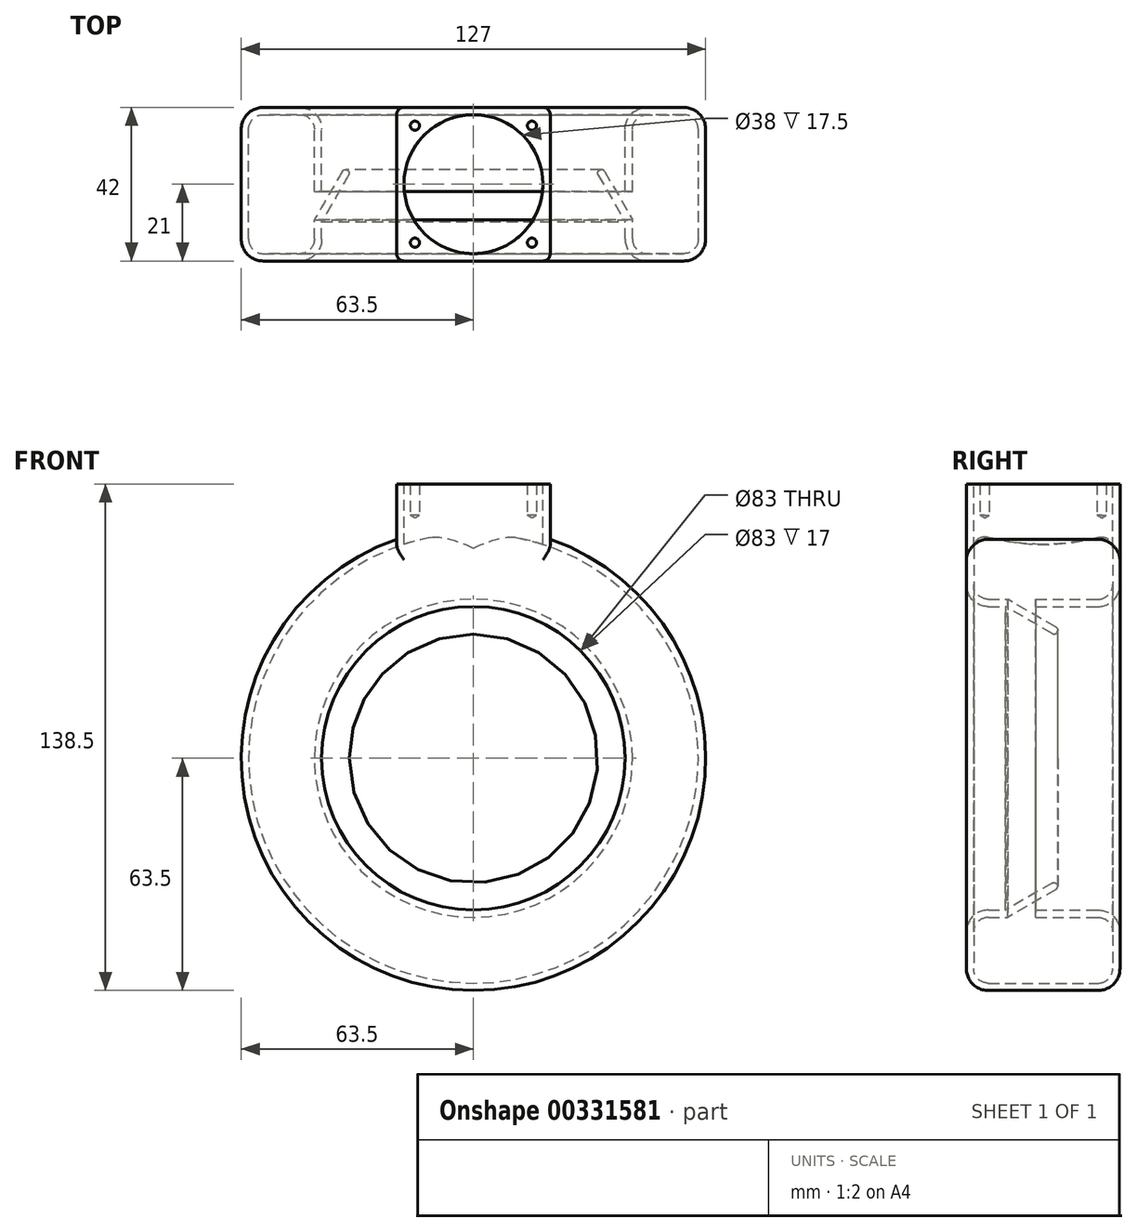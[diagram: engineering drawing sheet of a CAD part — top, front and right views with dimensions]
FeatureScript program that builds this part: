
annotation { "Feature Type Name" : "Feature", "Feature Type Description" : "" }
export const myFeature = defineFeature(function(context is Context, id is Id, definition is map)
    precondition{}
    {
        {
            var Q0;
            Q0=qCreatedBy(makeId("Top.planeOp"),FACE);
            var sketch = newSketch(context, id + "F0", { "sketchPlane" : qUnion([Q0])});
            skLineSegment(sketch, "E0.bottom", {"start": v(-7.5, 20) * mm, "end": v(2.5, 20) * mm, "construction": true});
            skLineSegment(sketch, "E0.top", {"start": v(-7.5, -20) * mm, "end": v(2.5, -20) * mm, "construction": true});
            skLineSegment(sketch, "E0.left", {"start": v(-12.5, 15) * mm, "end": v(-12.5, -15) * mm, "construction": true});
            skPoint(sketch, "E0.middle", {"position": v(0, 0) * mm});
            skPoint(sketch, "E1.visualSharp", {"position": v(-12.5, 20) * mm});
            skArc(sketch, "E1.filletArc", {"start": v(-7.5, 20) * mm, "mid": v(-11.04, 18.54) * mm, "end": v(-12.5, 15) * mm, "construction": true});
            skPoint(sketch, "E2.visualSharp", {"position": v(12.5, 20) * mm});
            skArc(sketch, "E2.filletArc", {"start": v(7.5, 15) * mm, "mid": v(6.04, 18.54) * mm, "end": v(2.5, 20) * mm, "construction": true});
            skPoint(sketch, "E3.visualSharp", {"position": v(12.5, -20) * mm});
            skArc(sketch, "E3.filletArc", {"start": v(2.5, -20) * mm, "mid": v(6.04, -18.54) * mm, "end": v(7.5, -15) * mm, "construction": true});
            skPoint(sketch, "E4.visualSharp", {"position": v(-12.5, -20) * mm});
            skArc(sketch, "E4.filletArc", {"start": v(-12.5, -15) * mm, "mid": v(-11.04, -18.54) * mm, "end": v(-7.5, -20) * mm, "construction": true});
            skLineSegment(sketch, "E5", {"start": v(7.5, -10) * mm, "end": v(15, 3) * mm, "construction": true});
            skLineSegment(sketch, "E6", {"start": v(7.5, 15) * mm, "end": v(7.5, -2) * mm, "construction": true});
            skLineSegment(sketch, "E7", {"start": v(7.5, -10) * mm, "end": v(7.5, -15) * mm, "construction": true});
            skLineSegment(sketch, "E8.0", {"start": v(8.5, 15) * mm, "end": v(8.5, -2) * mm});
            skArc(sketch, "E8.1", {"start": v(8.5, 15) * mm, "mid": v(6.74, 19.24) * mm, "end": v(2.5, 21) * mm});
            skLineSegment(sketch, "E8.2", {"start": v(-7.5, 21) * mm, "end": v(2.5, 21) * mm});
            skArc(sketch, "E8.3", {"start": v(-7.5, 21) * mm, "mid": v(-11.74, 19.24) * mm, "end": v(-13.5, 15) * mm});
            skLineSegment(sketch, "E8.4", {"start": v(-13.5, 15) * mm, "end": v(-13.5, -15) * mm});
            skArc(sketch, "E8.5", {"start": v(-13.5, -15) * mm, "mid": v(-11.74, -19.24) * mm, "end": v(-7.5, -21) * mm});
            skLineSegment(sketch, "E8.6", {"start": v(8.5, -10.27) * mm, "end": v(15.87, 2.5) * mm});
            skLineSegment(sketch, "E8.7", {"start": v(8.5, -10.27) * mm, "end": v(8.5, -15) * mm});
            skArc(sketch, "E8.8", {"start": v(2.5, -21) * mm, "mid": v(6.74, -19.24) * mm, "end": v(8.5, -15) * mm});
            skLineSegment(sketch, "E8.9", {"start": v(-7.5, -21) * mm, "end": v(2.5, -21) * mm});
            skLineSegment(sketch, "E9.0", {"start": v(6.5, 15) * mm, "end": v(6.5, -2) * mm});
            skArc(sketch, "E9.1", {"start": v(6.5, 15) * mm, "mid": v(5.33, 17.83) * mm, "end": v(2.5, 19) * mm});
            skLineSegment(sketch, "E9.2", {"start": v(-7.5, 19) * mm, "end": v(2.5, 19) * mm});
            skArc(sketch, "E9.3", {"start": v(-7.5, 19) * mm, "mid": v(-10.33, 17.83) * mm, "end": v(-11.5, 15) * mm});
            skLineSegment(sketch, "E9.4", {"start": v(-11.5, 15) * mm, "end": v(-11.5, -15) * mm});
            skArc(sketch, "E9.5", {"start": v(-11.5, -15) * mm, "mid": v(-10.33, -17.83) * mm, "end": v(-7.5, -19) * mm});
            skLineSegment(sketch, "E9.6", {"start": v(6.5, -9.73) * mm, "end": v(14.13, 3.5) * mm});
            skLineSegment(sketch, "E9.7", {"start": v(6.5, -9.73) * mm, "end": v(6.5, -15) * mm});
            skArc(sketch, "E9.8", {"start": v(2.5, -19) * mm, "mid": v(5.33, -17.83) * mm, "end": v(6.5, -15) * mm});
            skLineSegment(sketch, "E9.9", {"start": v(-7.5, -19) * mm, "end": v(2.5, -19) * mm});
            skLineSegment(sketch, "E10", {"start": v(6.5, -2) * mm, "end": v(8.5, -2) * mm});
            skArc(sketch, "E11", {"start": v(15.87, 2.5) * mm, "mid": v(15.5, 3.86) * mm, "end": v(14.13, 3.5) * mm});
            skSolve(sketch);
        }
        {
            var Q0;
            Q0=qCreatedBy(makeId("Front.planeOp"),FACE);
            var sketch = newSketch(context, id + "F1", { "sketchPlane" : qUnion([Q0])});
            skLineSegment(sketch, "E12", {"start": v(0, 0) * mm, "end": v(0, 0) * mm});
            skLineSegment(sketch, "E13", {"start": v(50, -50) * mm, "end": v(50, -50) * mm});
            skLineSegment(sketch, "E14", {"start": v(100, 0) * mm, "end": v(100, 0) * mm});
            skLineSegment(sketch, "E15", {"start": v(50, 50) * mm, "end": v(50, 50) * mm});
            skPoint(sketch, "E16.visualSharp", {"position": v(0, 50) * mm});
            skArc(sketch, "E16.filletArc", {"start": v(50, 50) * mm, "mid": v(14.64, 35.36) * mm, "end": v(0, 0) * mm});
            skPoint(sketch, "E17.visualSharp", {"position": v(100, 50) * mm});
            skArc(sketch, "E17.filletArc", {"start": v(100, 0) * mm, "mid": v(85.36, 35.36) * mm, "end": v(50, 50) * mm});
            skPoint(sketch, "E18.visualSharp", {"position": v(100, -50) * mm});
            skArc(sketch, "E18.filletArc", {"start": v(50, -50) * mm, "mid": v(85.36, -35.36) * mm, "end": v(100, 0) * mm});
            skPoint(sketch, "E19.visualSharp", {"position": v(0, -50) * mm});
            skArc(sketch, "E19.filletArc", {"start": v(0, 0) * mm, "mid": v(14.64, -35.36) * mm, "end": v(50, -50) * mm});
            skSolve(sketch);
        }
        {
            var Q0;
            Q0=makeQuery(id+"F0.imprint","IMPRINT",FACE,{"disambiguationData":[TD([[makeQuery(id+"F0.imprint","IMPRINT",EDGE,{"derivedFrom":sQuery(id+"F0.wireOp",EDGE,"E8.0")}),-1.0]])]});
            var Q1;
            Q1=sQuery(id+"F1.wireOp",EDGE,"E16.filletArc");
            var Q2;
            Q2=sQuery(id+"F1.wireOp",EDGE,"E18.filletArc");
            var Q3;
            Q3=sQuery(id+"F1.wireOp",EDGE,"E17.filletArc");
            var Q4;
            Q4=sQuery(id+"F1.wireOp",EDGE,"E19.filletArc");
            sweep(context, id + "F2", {"profiles" : qUnion([Q0]), "path" : qUnion([Q1, Q2, Q3, Q4])});
        }
        {
            var Q0;
            Q0=qCreatedBy(makeId("Top.planeOp"),FACE);
            cPlane(context, id + "F3", {"entities" : qUnion([Q0]), "cplaneType" : CPlaneType.OFFSET, "offset" : 75 * mm, "width" : 150 * mm, "height" : 150 * mm});
        }
        {
            var Q0;
            Q0=qCreatedBy(id+"F3.planeOp",FACE);
            var sketch = newSketch(context, id + "F4", { "sketchPlane" : qUnion([Q0])});
            skLineSegment(sketch, "E20.0", {"start": v(-13.5, 15) * mm, "end": v(113.5, 15) * mm, "construction": true});
            skLineSegment(sketch, "E20.1", {"start": v(-13.5, -15) * mm, "end": v(113.5, -15) * mm, "construction": true});
            skLineSegment(sketch, "E21", {"start": v(50, 49.18) * mm, "end": v(50, -47.1) * mm, "construction": true});
            skPoint(sketch, "E21.startSnap0", {"position": v(50, 15) * mm});
            skLineSegment(sketch, "E22", {"start": v(0, 0) * mm, "end": v(109, 0) * mm, "construction": true});
            skCircle(sketch, "E23", {"center": v(50, 0) * mm, "radius": 19 * mm});
            skLineSegment(sketch, "E24.bottom", {"start": v(71, -21) * mm, "end": v(29, -21) * mm});
            skLineSegment(sketch, "E24.top", {"start": v(71, 21) * mm, "end": v(29, 21) * mm});
            skLineSegment(sketch, "E24.left", {"start": v(71, -21) * mm, "end": v(71, 21) * mm});
            skLineSegment(sketch, "E24.right", {"start": v(29, -21) * mm, "end": v(29, 21) * mm});
            skSolve(sketch);
        }
        {
            var Q0;
            Q0 = qSketchRegion(id + "F4", true);
            extrude(context, id + "F5", {"entities" : qUnion([Q0]), "operationType" : NewBodyOperationType.ADD, "endBound" : BoundingType.UP_TO_NEXT, "oppositeDirection" : true, "depth" : 25 * mm});
        }
        {
            var Q0;
            Q0=makeQuery(id+"F5.opExtrude","CAP_FACE",FACE,{"disambiguationData":[OSD([sQuery(id+"F4.wireOp",EDGE,"E23"),sQuery(id+"F4.wireOp",EDGE,"E24.bottom"),sQuery(id+"F4.wireOp",EDGE,"E24.top"),sQuery(id+"F4.wireOp",EDGE,"E24.left"),sQuery(id+"F4.wireOp",EDGE,"E24.right")])],"isStart":true});
            var sketch = newSketch(context, id + "F6", { "sketchPlane" : qUnion([Q0])});
            skCircle(sketch, "E25.0", {"center": v(50, 0) * mm, "radius": 19 * mm});
            skSolve(sketch);
        }
        {
            var Q0;
            Q0 = qSketchRegion(id + "F6", true);
            extrude(context, id + "F7", {"entities" : qUnion([Q0]), "operationType" : NewBodyOperationType.REMOVE, "oppositeDirection" : true, "depth" : 25 * mm});
        }
        {
            var Q0;
            Q0=makeQuery(id+"F5.opExtrude","CAP_FACE",FACE,{"disambiguationData":[OSD([sQuery(id+"F4.wireOp",EDGE,"E23"),sQuery(id+"F4.wireOp",EDGE,"E24.bottom"),sQuery(id+"F4.wireOp",EDGE,"E24.top"),sQuery(id+"F4.wireOp",EDGE,"E24.left"),sQuery(id+"F4.wireOp",EDGE,"E24.right")])],"isStart":true});
            var sketch = newSketch(context, id + "F8", { "sketchPlane" : qUnion([Q0])});
            skCircle(sketch, "E26.0", {"center": v(50, 0) * mm, "radius": 19 * mm, "construction": true});
            skLineSegment(sketch, "E27.bottom", {"start": v(66, 16) * mm, "end": v(34, 16) * mm, "construction": true});
            skLineSegment(sketch, "E27.top", {"start": v(66, -16) * mm, "end": v(34, -16) * mm, "construction": true});
            skLineSegment(sketch, "E27.left", {"start": v(66, 16) * mm, "end": v(66, -16) * mm, "construction": true});
            skLineSegment(sketch, "E27.right", {"start": v(34, 16) * mm, "end": v(34, -16) * mm, "construction": true});
            skPoint(sketch, "E28", {"position": v(34, 16) * mm});
            skPoint(sketch, "E29", {"position": v(66, 16) * mm});
            skPoint(sketch, "E30", {"position": v(66, -16) * mm});
            skPoint(sketch, "E31", {"position": v(34, -16) * mm});
            skSolve(sketch);
        }
        {
            var Q0;
            Q0=sQuery(id+"F8.wireOp",VERTEX,"E27.bottom.end");
            var Q1;
            Q1=sQuery(id+"F8.wireOp",VERTEX,"E29");
            var Q2;
            Q2=sQuery(id+"F8.wireOp",VERTEX,"E30");
            var Q3;
            Q3=sQuery(id+"F8.wireOp",VERTEX,"E31");
            var Q4;
            Q4=makeQuery(id+"F2.opSweep","SWEPT_BODY",BODY,{"disambiguationData":[OSD([sQuery(id+"F0.wireOp",EDGE,"E8.0"),sQuery(id+"F0.wireOp",EDGE,"E8.1"),sQuery(id+"F0.wireOp",EDGE,"E8.2"),sQuery(id+"F0.wireOp",EDGE,"E8.3"),sQuery(id+"F0.wireOp",EDGE,"E8.4"),sQuery(id+"F0.wireOp",EDGE,"E8.5"),sQuery(id+"F0.wireOp",EDGE,"E8.6"),sQuery(id+"F0.wireOp",EDGE,"E8.8"),sQuery(id+"F0.wireOp",EDGE,"E8.9"),sQuery(id+"F0.wireOp",EDGE,"E9.0"),sQuery(id+"F0.wireOp",EDGE,"E9.1"),sQuery(id+"F0.wireOp",EDGE,"E9.2"),sQuery(id+"F0.wireOp",EDGE,"E9.3"),sQuery(id+"F0.wireOp",EDGE,"E9.4"),sQuery(id+"F0.wireOp",EDGE,"E9.5"),sQuery(id+"F0.wireOp",EDGE,"E9.6"),sQuery(id+"F0.wireOp",EDGE,"E9.8"),sQuery(id+"F0.wireOp",EDGE,"E9.9"),sQuery(id+"F0.wireOp",EDGE,"E10"),sQuery(id+"F0.wireOp",EDGE,"E9.7"),sQuery(id+"F0.wireOp",EDGE,"E8.7"),sQuery(id+"F0.wireOp",EDGE,"E11"),sQuery(id+"F1.wireOp",EDGE,"E19.filletArc")])]});
            hole(context, id + "F9", {"style" : HoleStyle.SIMPLE, "endStyle" : HoleEndStyle.BLIND, "standardTappedOrClearance" : lookupTablePath({ "standard" : "ISO", "engagement" : "75%", "pitch" : "0.5 mm", "size" : "M3", "type" : "Tapped" }), "standardBlindInLast" : lookupTablePath({ "standard" : "ISO", "engagement" : "75%", "pitch" : "0.5 mm", "size" : "M3", "type" : "Tapped" }), "holeDiameter" : 2.5 * mm, "showTappedDepth" : true, "holeDepth" : 8.5 * mm, "tappedDepth" : 7 * mm, "tapClearance" : 3, "startFromSketch" : true, "locations" : qUnion([Q0, Q1, Q2, Q3]), "scope" : qUnion([Q4]), "majorDiameter" : 3 * mm});
        }
        {
            var Q0;
            Q0=makeQuery(id+"F5.opExtrude","TWEAK_EDGE",EDGE,{"derivedFrom":[makeQuery(id+"F2.opSweep","SWEPT_FACE",FACE,{"disambiguationData":[OSD([sQuery(id+"F0.wireOp",EDGE,"E8.4"),sQuery(id+"F1.wireOp",EDGE,"E16.filletArc")])]}),makeQuery(id+"F4.imprint","IMPRINT",EDGE,{"derivedFrom":sQuery(id+"F4.wireOp",EDGE,"E24.left")})]});
            var Q1;
            Q1=makeQuery(id+"F5.opExtrude","SWEPT_EDGE",EDGE,{"disambiguationData":[OSD([sQuery(id+"F4.wireOp",EDGE,"E24.top"),sQuery(id+"F4.wireOp",EDGE,"E24.left")])]});
            var Q2;
            Q2=makeQuery(id+"F5.opExtrude","SWEPT_EDGE",EDGE,{"disambiguationData":[OSD([sQuery(id+"F4.wireOp",EDGE,"E24.bottom"),sQuery(id+"F4.wireOp",EDGE,"E24.left")])]});
            var Q3;
            Q3=makeQuery(id+"F5.opExtrude","SWEPT_EDGE",EDGE,{"disambiguationData":[OSD([sQuery(id+"F4.wireOp",EDGE,"E24.top"),sQuery(id+"F4.wireOp",EDGE,"E24.right")])]});
            var Q4;
            Q4=makeQuery(id+"F5.opExtrude","TWEAK_EDGE",EDGE,{"derivedFrom":[makeQuery(id+"F2.opSweep","SWEPT_FACE",FACE,{"disambiguationData":[OSD([sQuery(id+"F0.wireOp",EDGE,"E8.4"),sQuery(id+"F1.wireOp",EDGE,"E16.filletArc")])]}),makeQuery(id+"F4.imprint","IMPRINT",EDGE,{"derivedFrom":sQuery(id+"F4.wireOp",EDGE,"E24.right")})]});
            var Q5;
            Q5=makeQuery(id+"F5.opExtrude","SWEPT_EDGE",EDGE,{"disambiguationData":[OSD([sQuery(id+"F4.wireOp",EDGE,"E24.bottom"),sQuery(id+"F4.wireOp",EDGE,"E24.right")])]});
            fillet(context, id + "F10", {"entities" : qUnion([Q0, Q1, Q2, Q3, Q4, Q5]), "radius" : 2 * mm, "tangentPropagation" : true, "allowEdgeOverflow" : false});
        }
    });
